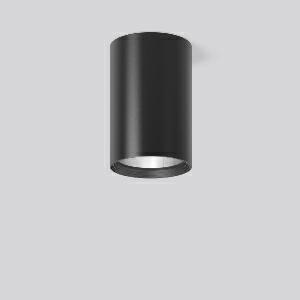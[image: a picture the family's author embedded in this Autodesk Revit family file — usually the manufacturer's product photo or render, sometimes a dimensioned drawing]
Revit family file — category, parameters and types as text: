
# Revit family: heledon_maxi_a_931244_003_2_f02c
name_source: partatom
category: Lighting Fixtures
units: mm (PartAtom-declared; Revit-internal decimal feet)

## family parameters
Cut with Voids When Loaded = No
Host = Face
Light Source = No
Part Type = Normal
Room Calculation Point = No
Round Connector Dimension = Use Diameter
Shared = No

## types (1)
- HELEDON maxi A (1 x LED Modul 927 bakery, 3300 lm, 2700)
    Apparent Load = 33 VA
    Approval mark = CE
    CIE Flux Codes = 100 100 100 100 100
    Color Rendering = 90
    Color Temperature = 2700
    Default Elevation = 1800 mm
    Description = Series: HELEDON maxi
Cylindrical surface-mounted downlight. Housing: die-cast aluminium, powder-coated. Internal ceiling frame polycarbonate with bayonet mounting. Black plastic ring and recessed LED to prevent glare from the side. Optical assembly with reflector made of MIRO-Silver with 98% total light reflection for outstanding efficiency - can be changed without tools. Special LED for illumination of pastries included. Suitable for Ceiling mounting. Easy installation with a separate ceiling frame with bayonet mounting and plug connection. Driver integrated. Connected via plug-in connector. High quality converter without flickering and stroboscopic effect. The following accessories can be mounted without use of tools: interchangeable lenses, decorative glasses, honeycomb louvre, clear and frosted diffusers, white interchangeable plastic ring. 
Colour: deep black, matt (RAL 9005)
Diameter: 123 mm
Height: 183 mm
Lamp: LED
Socket: without socket
Colour temperature: bakery
Colour rendering index (CRI): 97
System power: 33 W
Rated luminous flux: 3300 lm
Luminous efficiency: 100 lm/W
Control gear: Regulated power supply
Protection class: I
Type of protection: IP 20
    Height = 183 mm
    Lamp = 1 x LED Modul 927 bakery
    Lamp Light Flux = 3300 lm
    Lamp count = 1
    Length = 123 mm
    Lifetime = 50000 h
    Luminous efficacy = 100 lm/W
    Manufacturer = RZB
    ModVariant = No
    Model = 931244.003.2
    Mounting Place = Ceiling
    Mounting Type = Surface mounted
    Number of Poles = 1
    OnlyDefault = Yes
    Power Factor = 1
    Product Name = HELEDON maxi A
    Product group = Surface mounted downlights
    ProductGroupID = 302
    Protection Class = Protection class I
    Protection Degree = IP 20
    RLX_Detail_Level = 1
    RLX_Emergency_Light_Flux = 0 lm
    RLX_Emergency_Type = 0
    RLX_Emergency_Type_DB = No
    RlxData = <blob elided: 97245 chars, md5=9c4df3ab>
    Socket = socket
    Standby Power = 0 W
    System Light Flux = 3300 lm
    System Power = 33 W
    Type Comments = Product without accessories
    Type Image = 931192.003.jpg
    URL = http://relux.com
    VarID = ---
    Voltage = 230 V
    Voltage Range = 220-240 V
    Weight = 0.00 kg
    Width = 0 mm  [stored 0 ft]

note: [stored X ft] marks values corroborated as IEEE doubles in the binary element streams (Revit-internal decimal feet)

## geometry (parser evidence)
native form markers: Blend x4, Sweep x10
no freeform markers — native parametric forms only
